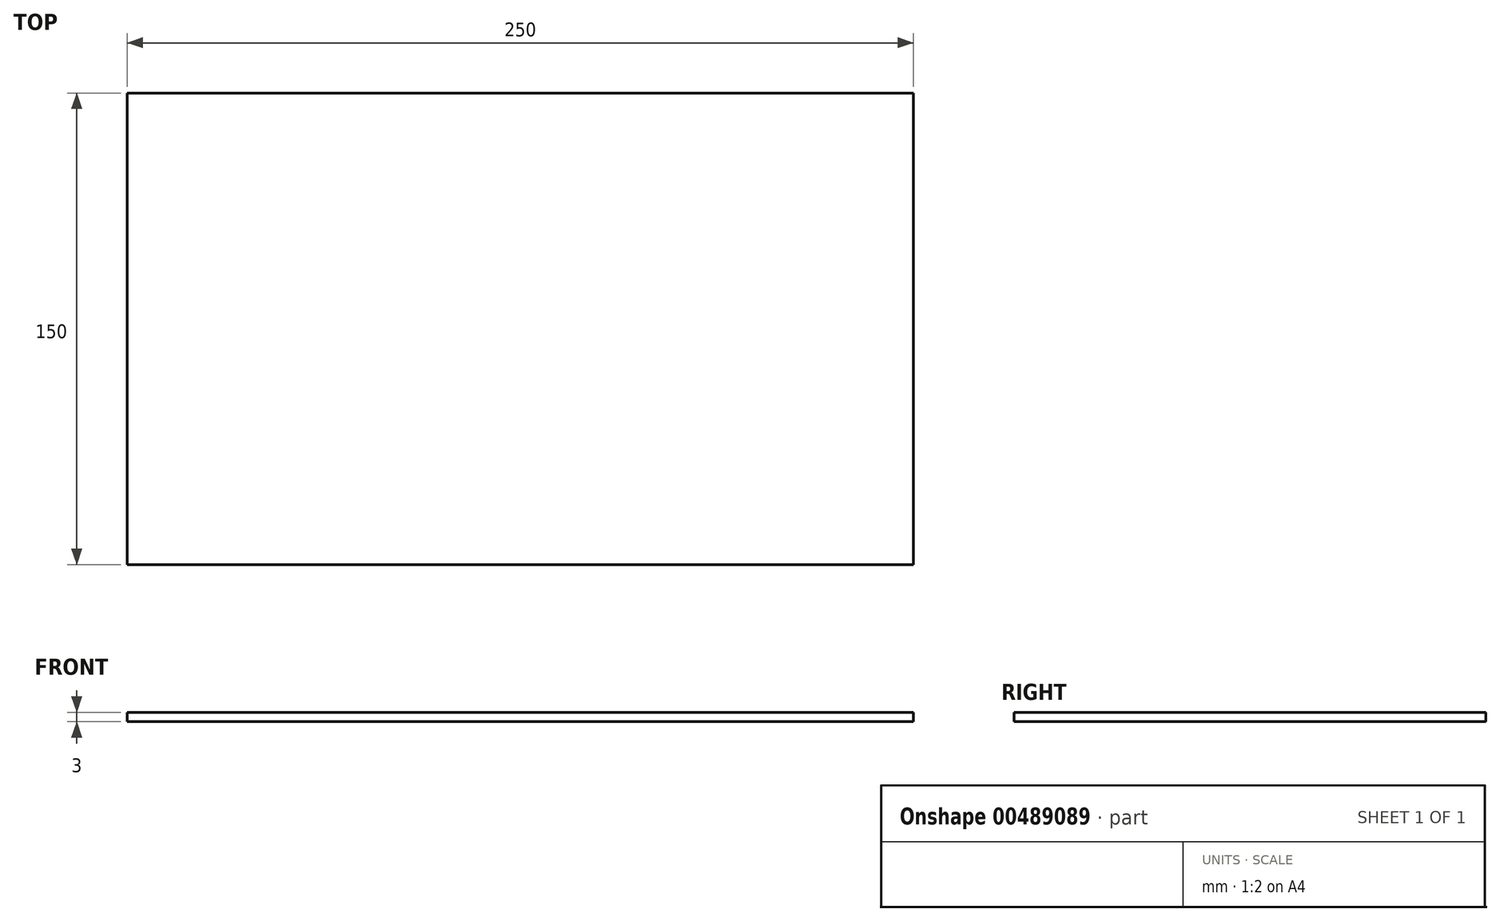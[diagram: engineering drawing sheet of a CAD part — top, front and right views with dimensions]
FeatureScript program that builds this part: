
annotation { "Feature Type Name" : "Feature", "Feature Type Description" : "" }
export const myFeature = defineFeature(function(context is Context, id is Id, definition is map)
    precondition{}
    {
        {
            var Q0;
            Q0=qCreatedBy(makeId("Top.planeOp"),FACE);
            var sketch = newSketch(context, id + "F0", { "sketchPlane" : qUnion([Q0])});
            skLineSegment(sketch, "E0.bottom", {"start": v(-130.89, 66.9) * mm, "end": v(119.11, 66.9) * mm});
            skLineSegment(sketch, "E0.top", {"start": v(-130.89, -83.1) * mm, "end": v(119.11, -83.1) * mm});
            skLineSegment(sketch, "E0.left", {"start": v(-130.89, 66.9) * mm, "end": v(-130.89, -83.1) * mm});
            skLineSegment(sketch, "E0.right", {"start": v(119.11, 66.9) * mm, "end": v(119.11, -83.1) * mm});
            skSolve(sketch);
        }
        {
            var Q0;
            Q0=makeQuery(id+"F0.imprint","IMPRINT",FACE,{"disambiguationData":[TD([[makeQuery(id+"F0.imprint","IMPRINT",EDGE,{"derivedFrom":sQuery(id+"F0.wireOp",EDGE,"E0.bottom")}),-1.0]])]});
            extrude(context, id + "F1", {"entities" : qUnion([Q0]), "depth" : 3 * mm});
        }
    });
